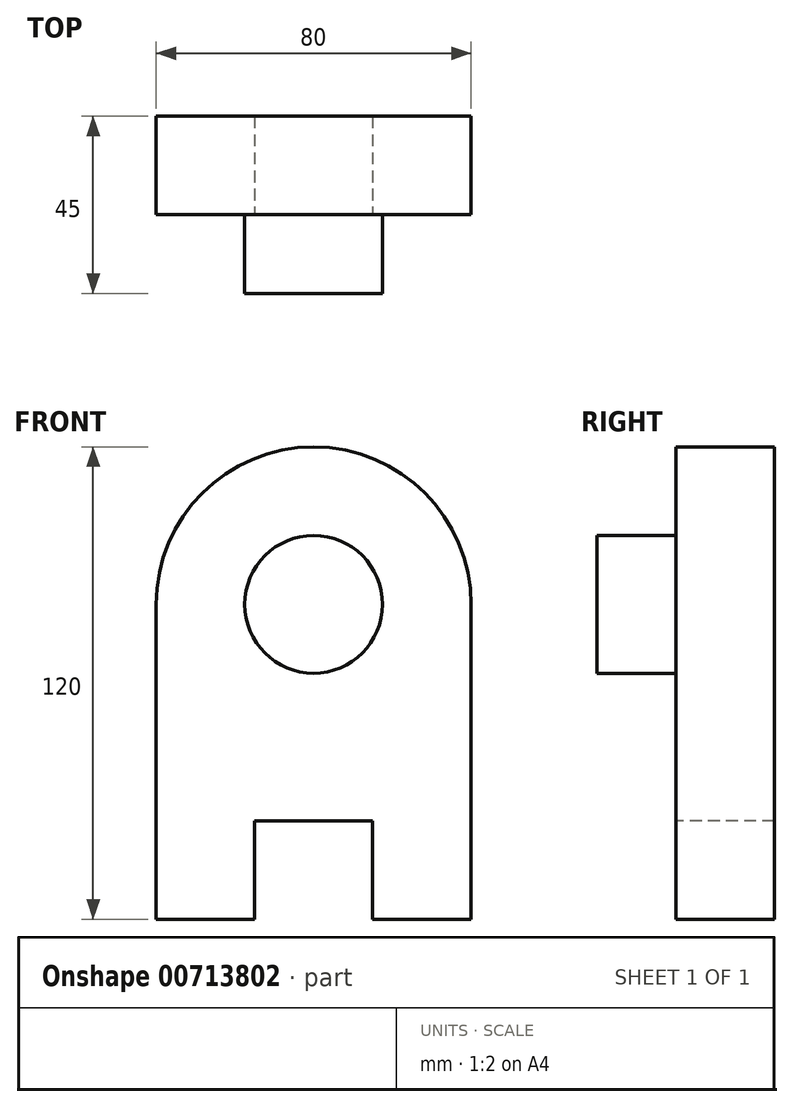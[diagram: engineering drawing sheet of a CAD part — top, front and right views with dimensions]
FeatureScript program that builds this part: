
annotation { "Feature Type Name" : "Feature", "Feature Type Description" : "" }
export const myFeature = defineFeature(function(context is Context, id is Id, definition is map)
    precondition{}
    {
        {
            var Q0;
            Q0=qCreatedBy(makeId("Front.planeOp"),FACE);
            var sketch = newSketch(context, id + "F0", { "sketchPlane" : qUnion([Q0])});
            skLineSegment(sketch, "E0.bottom", {"start": v(40, -60) * mm, "end": v(-40, -60) * mm});
            skLineSegment(sketch, "E0.top", {"start": v(40, 60) * mm, "end": v(-40, 60) * mm});
            skLineSegment(sketch, "E0.left", {"start": v(40, -60) * mm, "end": v(40, 60) * mm});
            skLineSegment(sketch, "E0.right", {"start": v(-40, -60) * mm, "end": v(-40, 60) * mm});
            skPoint(sketch, "E0.middle", {"position": v(0, 0) * mm});
            skSolve(sketch);
        }
        {
            var Q0;
            Q0=makeQuery(id+"F0.imprint","IMPRINT",FACE,{"disambiguationData":[TD([[makeQuery(id+"F0.imprint","IMPRINT",EDGE,{"derivedFrom":sQuery(id+"F0.wireOp",EDGE,"E0.bottom")}),-1.0]])]});
            extrude(context, id + "F1", {"entities" : qUnion([Q0]), "depth" : 25 * mm, "offsetDistance" : 25 * mm});
        }
        {
            var Q0;
            Q0=makeQuery(id+"F1.opExtrude","SWEPT_EDGE",EDGE,{"disambiguationData":[OSD([sQuery(id+"F0.wireOp",EDGE,"E0.top"),sQuery(id+"F0.wireOp",EDGE,"E0.left")])]});
            var Q1;
            Q1=makeQuery(id+"F1.opExtrude","SWEPT_EDGE",EDGE,{"disambiguationData":[OSD([sQuery(id+"F0.wireOp",EDGE,"E0.top"),sQuery(id+"F0.wireOp",EDGE,"E0.right")])]});
            fillet(context, id + "F2", {"entities" : qUnion([Q0, Q1]), "radius" : 40 * mm, "tangentPropagation" : true, "allowEdgeOverflow" : false});
        }
        {
            var Q0;
            Q0=makeQuery(id+"F1.opExtrude","CAP_FACE",FACE,{"disambiguationData":[OSD([sQuery(id+"F0.wireOp",EDGE,"E0.bottom"),sQuery(id+"F0.wireOp",EDGE,"E0.top"),sQuery(id+"F0.wireOp",EDGE,"E0.left"),sQuery(id+"F0.wireOp",EDGE,"E0.right")])],"isStart":false});
            var sketch = newSketch(context, id + "F3", { "sketchPlane" : qUnion([Q0])});
            skLineSegment(sketch, "E1.bottom", {"start": v(-15, -85) * mm, "end": v(15, -85) * mm});
            skLineSegment(sketch, "E1.top", {"start": v(-15, -35) * mm, "end": v(15, -35) * mm});
            skLineSegment(sketch, "E1.left", {"start": v(-15, -85) * mm, "end": v(-15, -35) * mm});
            skLineSegment(sketch, "E1.right", {"start": v(15, -85) * mm, "end": v(15, -35) * mm});
            skPoint(sketch, "E1.middle", {"position": v(0, -60) * mm});
            skSolve(sketch);
        }
        {
            var Q0;
            Q0 = qSketchRegion(id + "F3", true);
            extrude(context, id + "F4", {"entities" : qUnion([Q0]), "operationType" : NewBodyOperationType.REMOVE, "endBound" : BoundingType.THROUGH_ALL, "oppositeDirection" : true, "depth" : 25 * mm, "offsetDistance" : 25 * mm});
        }
        {
            var Q0;
            Q0=makeQuery(id+"F1.opExtrude","CAP_FACE",FACE,{"disambiguationData":[OSD([sQuery(id+"F0.wireOp",EDGE,"E0.bottom"),sQuery(id+"F0.wireOp",EDGE,"E0.top"),sQuery(id+"F0.wireOp",EDGE,"E0.left"),sQuery(id+"F0.wireOp",EDGE,"E0.right")])],"isStart":false});
            var sketch = newSketch(context, id + "F5", { "sketchPlane" : qUnion([Q0])});
            skCircle(sketch, "E2", {"center": v(0, 20) * mm, "radius": 17.5 * mm});
            skSolve(sketch);
        }
        {
            var Q0;
            Q0 = qSketchRegion(id + "F5", true);
            extrude(context, id + "F6", {"entities" : qUnion([Q0]), "operationType" : NewBodyOperationType.ADD, "depth" : 20 * mm, "offsetDistance" : 25 * mm});
        }
    });
